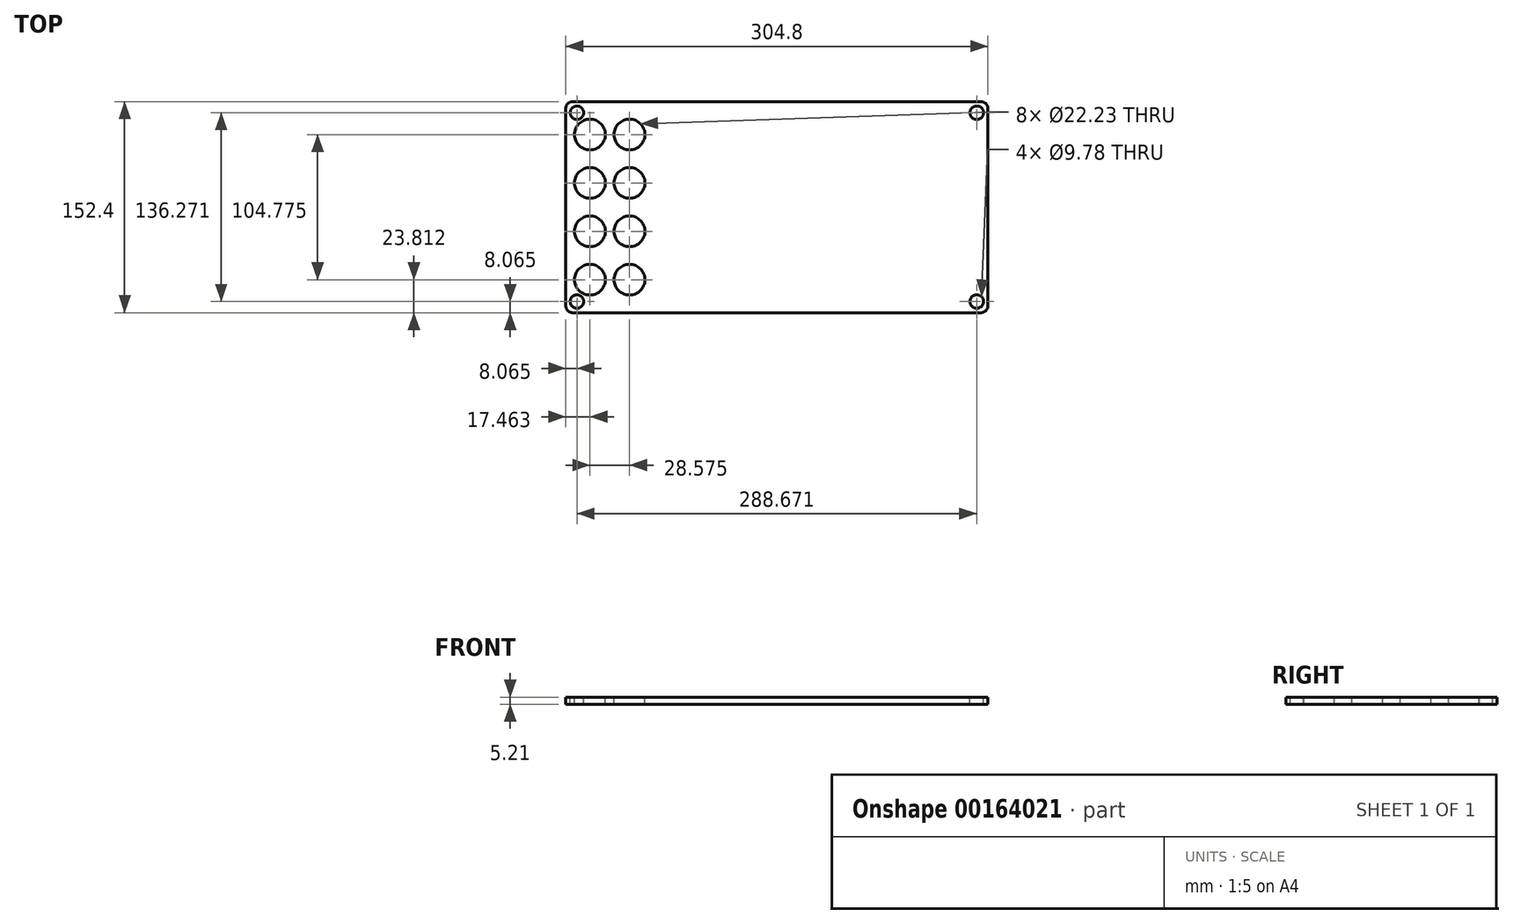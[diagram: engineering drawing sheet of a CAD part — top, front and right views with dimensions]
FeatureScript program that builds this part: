
annotation { "Feature Type Name" : "Feature", "Feature Type Description" : "" }
export const myFeature = defineFeature(function(context is Context, id is Id, definition is map)
    precondition{}
    {
        {
            var Q0;
            Q0=qCreatedBy(makeId("Top.planeOp"),FACE);
            var sketch = newSketch(context, id + "F0", { "sketchPlane" : qUnion([Q0])});
            skLineSegment(sketch, "E0.bottom", {"start": v(152.4, -76.2) * mm, "end": v(-152.4, -76.2) * mm});
            skLineSegment(sketch, "E0.top", {"start": v(152.4, 76.2) * mm, "end": v(-152.4, 76.2) * mm});
            skLineSegment(sketch, "E0.left", {"start": v(152.4, -76.2) * mm, "end": v(152.4, 76.2) * mm});
            skLineSegment(sketch, "E0.right", {"start": v(-152.4, -76.2) * mm, "end": v(-152.4, 76.2) * mm});
            skPoint(sketch, "E0.middle", {"position": v(0, 0) * mm});
            skSolve(sketch);
        }
        {
            var Q0;
            Q0=makeQuery(id+"F0.imprint","IMPRINT",FACE,{"disambiguationData":[TD([[makeQuery(id+"F0.imprint","IMPRINT",EDGE,{"derivedFrom":sQuery(id+"F0.wireOp",EDGE,"E0.bottom")}),-1.0]])]});
            extrude(context, id + "F1", {"entities" : qUnion([Q0]), "depth" : 5.2 * mm});
        }
        {
            var Q0;
            Q0=makeQuery(id+"F1.opExtrude","SWEPT_EDGE",EDGE,{"disambiguationData":[OSD([sQuery(id+"F0.wireOp",EDGE,"E0.top"),sQuery(id+"F0.wireOp",EDGE,"E0.right")])]});
            var Q1;
            Q1=makeQuery(id+"F1.opExtrude","SWEPT_EDGE",EDGE,{"disambiguationData":[OSD([sQuery(id+"F0.wireOp",EDGE,"E0.bottom"),sQuery(id+"F0.wireOp",EDGE,"E0.right")])]});
            var Q2;
            Q2=makeQuery(id+"F1.opExtrude","SWEPT_EDGE",EDGE,{"disambiguationData":[OSD([sQuery(id+"F0.wireOp",EDGE,"E0.top"),sQuery(id+"F0.wireOp",EDGE,"E0.left")])]});
            var Q3;
            Q3=makeQuery(id+"F1.opExtrude","SWEPT_EDGE",EDGE,{"disambiguationData":[OSD([sQuery(id+"F0.wireOp",EDGE,"E0.bottom"),sQuery(id+"F0.wireOp",EDGE,"E0.left")])]});
            fillet(context, id + "F2", {"entities" : qUnion([Q0, Q1, Q2, Q3]), "radius" : 5.08 * mm, "tangentPropagation" : true, "allowEdgeOverflow" : false});
        }
        {
            var Q0;
            Q0=makeQuery(id+"F1.opExtrude","CAP_FACE",FACE,{"disambiguationData":[OSD([sQuery(id+"F0.wireOp",EDGE,"E0.bottom"),sQuery(id+"F0.wireOp",EDGE,"E0.top"),sQuery(id+"F0.wireOp",EDGE,"E0.left"),sQuery(id+"F0.wireOp",EDGE,"E0.right")])],"isStart":false});
            var sketch = newSketch(context, id + "F3", { "sketchPlane" : qUnion([Q0])});
            skCircle(sketch, "E1", {"center": v(-144.34, 68.14) * mm, "radius": 4.89 * mm});
            skCircle(sketch, "E2", {"center": v(-144.34, -68.14) * mm, "radius": 4.89 * mm});
            skCircle(sketch, "E3", {"center": v(144.34, 68.14) * mm, "radius": 4.89 * mm});
            skCircle(sketch, "E4", {"center": v(144.34, -68.14) * mm, "radius": 4.89 * mm});
            skSolve(sketch);
        }
        {
            var Q0;
            Q0 = qSketchRegion(id + "F3", true);
            extrude(context, id + "F4", {"entities" : qUnion([Q0]), "operationType" : NewBodyOperationType.REMOVE, "endBound" : BoundingType.THROUGH_ALL, "oppositeDirection" : true, "depth" : 3.17 * mm});
        }
        {
            var Q0;
            Q0=makeQuery(id+"F1.opExtrude","CAP_FACE",FACE,{"disambiguationData":[OSD([sQuery(id+"F0.wireOp",EDGE,"E0.bottom"),sQuery(id+"F0.wireOp",EDGE,"E0.top"),sQuery(id+"F0.wireOp",EDGE,"E0.left"),sQuery(id+"F0.wireOp",EDGE,"E0.right")])],"isStart":false});
            var sketch = newSketch(context, id + "F5", { "sketchPlane" : qUnion([Q0])});
            skCircle(sketch, "E5", {"center": v(-134.94, 52.39) * mm, "radius": 11.11 * mm});
            skCircle(sketch, "E6", {"center": v(-106.36, 52.39) * mm, "radius": 11.11 * mm});
            skCircle(sketch, "E7", {"center": v(-134.94, 17.46) * mm, "radius": 11.11 * mm});
            skCircle(sketch, "E8", {"center": v(-106.36, 17.46) * mm, "radius": 11.11 * mm});
            skCircle(sketch, "E9", {"center": v(-134.94, -17.46) * mm, "radius": 11.11 * mm});
            skCircle(sketch, "E10", {"center": v(-106.36, -17.46) * mm, "radius": 11.11 * mm});
            skCircle(sketch, "E11", {"center": v(-134.94, -52.39) * mm, "radius": 11.11 * mm});
            skCircle(sketch, "E12", {"center": v(-106.36, -52.39) * mm, "radius": 11.11 * mm});
            skSolve(sketch);
        }
        {
            var Q0;
            Q0=makeQuery(id+"F5.imprint","IMPRINT",FACE,{"disambiguationData":[TD([[makeQuery(id+"F5.imprint","IMPRINT",EDGE,{"derivedFrom":sQuery(id+"F5.wireOp",EDGE,"E12")}),1.0]])]});
            var Q1;
            Q1=makeQuery(id+"F5.imprint","IMPRINT",FACE,{"disambiguationData":[TD([[makeQuery(id+"F5.imprint","IMPRINT",EDGE,{"derivedFrom":sQuery(id+"F5.wireOp",EDGE,"E11")}),1.0]])]});
            var Q2;
            Q2=makeQuery(id+"F5.imprint","IMPRINT",FACE,{"disambiguationData":[TD([[makeQuery(id+"F5.imprint","IMPRINT",EDGE,{"derivedFrom":sQuery(id+"F5.wireOp",EDGE,"E9")}),1.0]])]});
            var Q3;
            Q3=makeQuery(id+"F5.imprint","IMPRINT",FACE,{"disambiguationData":[TD([[makeQuery(id+"F5.imprint","IMPRINT",EDGE,{"derivedFrom":sQuery(id+"F5.wireOp",EDGE,"E10")}),1.0]])]});
            var Q4;
            Q4=makeQuery(id+"F5.imprint","IMPRINT",FACE,{"disambiguationData":[TD([[makeQuery(id+"F5.imprint","IMPRINT",EDGE,{"derivedFrom":sQuery(id+"F5.wireOp",EDGE,"E7")}),1.0]])]});
            var Q5;
            Q5=makeQuery(id+"F5.imprint","IMPRINT",FACE,{"disambiguationData":[TD([[makeQuery(id+"F5.imprint","IMPRINT",EDGE,{"derivedFrom":sQuery(id+"F5.wireOp",EDGE,"E8")}),1.0]])]});
            var Q6;
            Q6=makeQuery(id+"F5.imprint","IMPRINT",FACE,{"disambiguationData":[TD([[makeQuery(id+"F5.imprint","IMPRINT",EDGE,{"derivedFrom":sQuery(id+"F5.wireOp",EDGE,"E5")}),1.0]])]});
            var Q7;
            Q7=makeQuery(id+"F5.imprint","IMPRINT",FACE,{"disambiguationData":[TD([[makeQuery(id+"F5.imprint","IMPRINT",EDGE,{"derivedFrom":sQuery(id+"F5.wireOp",EDGE,"E6")}),1.0]])]});
            extrude(context, id + "F6", {"entities" : qUnion([Q0, Q1, Q2, Q3, Q4, Q5, Q6, Q7]), "operationType" : NewBodyOperationType.REMOVE, "endBound" : BoundingType.THROUGH_ALL, "oppositeDirection" : true, "depth" : 25.4 * mm});
        }
    });
